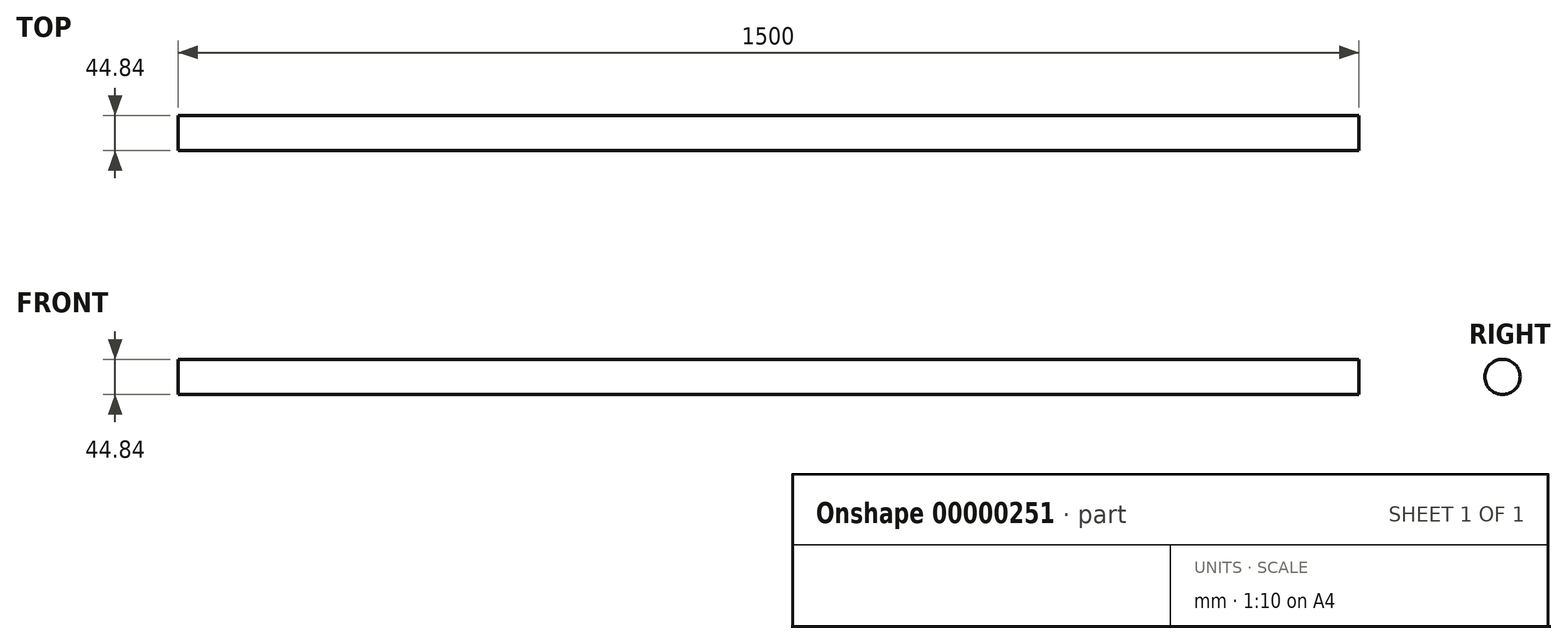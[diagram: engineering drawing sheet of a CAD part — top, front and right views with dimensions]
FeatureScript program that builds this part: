
annotation { "Feature Type Name" : "Feature", "Feature Type Description" : "" }
export const myFeature = defineFeature(function(context is Context, id is Id, definition is map)
    precondition{}
    {
        {
            var Q0;
            Q0=qCreatedBy(makeId("Right.planeOp"),FACE);
            var sketch = newSketch(context, id + "F0", { "sketchPlane" : qUnion([Q0])});
            skCircle(sketch, "E0", {"center": v(0, 0) * mm, "radius": 22.42 * mm});
            skSolve(sketch);
        }
        {
            var Q0;
            Q0=makeQuery(id+"F0.imprint","IMPRINT",FACE,{"disambiguationData":[TD([[makeQuery(id+"F0.imprint","IMPRINT",EDGE,{"derivedFrom":sQuery(id+"F0.wireOp",EDGE,"E0")}),1.0]])]});
            extrude(context, id + "F1", {"entities" : qUnion([Q0]), "depth" : 1500 * mm});
        }
    });
